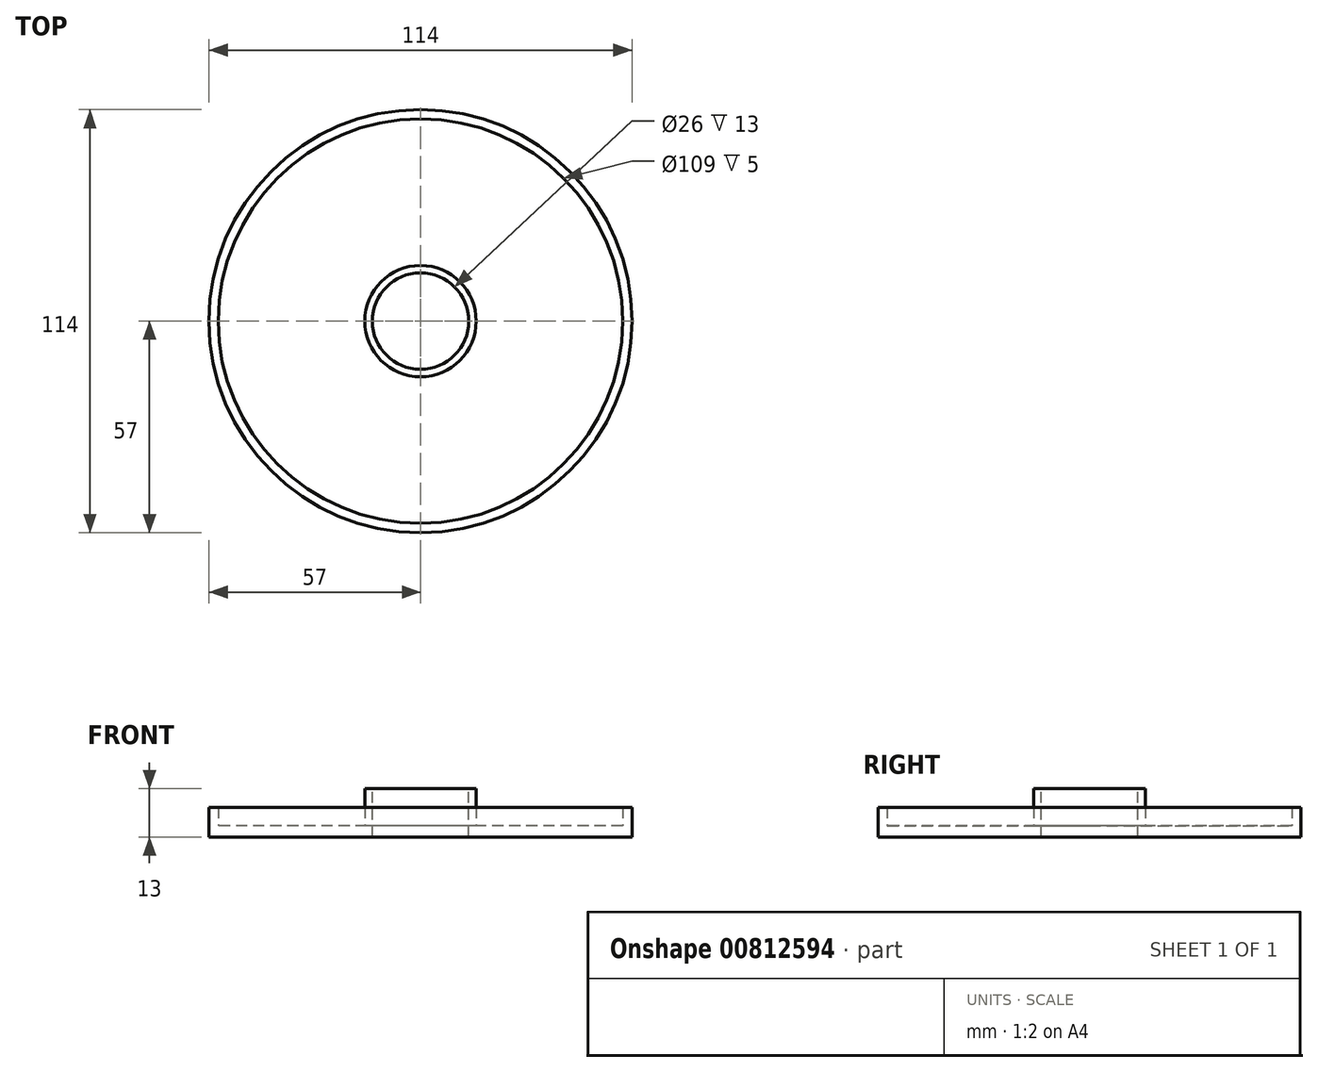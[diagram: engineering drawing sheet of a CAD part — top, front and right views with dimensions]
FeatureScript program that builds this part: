
annotation { "Feature Type Name" : "Feature", "Feature Type Description" : "" }
export const myFeature = defineFeature(function(context is Context, id is Id, definition is map)
    precondition{}
    {
        {
            var Q0;
            Q0=qCreatedBy(makeId("Top.planeOp"),FACE);
            var sketch = newSketch(context, id + "F0", { "sketchPlane" : qUnion([Q0])});
            skCircle(sketch, "E0", {"center": v(0, 0) * mm, "radius": 54.5 * mm});
            skCircle(sketch, "E1", {"center": v(0, 0) * mm, "radius": 57 * mm});
            skCircle(sketch, "E2", {"center": v(0, 0) * mm, "radius": 13 * mm});
            skCircle(sketch, "E3", {"center": v(0, 0) * mm, "radius": 15 * mm});
            skSolve(sketch);
        }
        {
            var Q0;
            Q0=makeQuery(id+"F0.imprint","IMPRINT",FACE,{"disambiguationData":[TD([[makeQuery(id+"F0.imprint","IMPRINT",EDGE,{"derivedFrom":sQuery(id+"F0.wireOp",EDGE,"E0")}),1.0]])]});
            var Q1;
            Q1=makeQuery(id+"F0.imprint","IMPRINT",FACE,{"disambiguationData":[TD([[makeQuery(id+"F0.imprint","IMPRINT",EDGE,{"derivedFrom":sQuery(id+"F0.wireOp",EDGE,"E0")}),-1.0]])]});
            var Q2;
            Q2=makeQuery(id+"F0.imprint","IMPRINT",FACE,{"disambiguationData":[TD([[makeQuery(id+"F0.imprint","IMPRINT",EDGE,{"derivedFrom":sQuery(id+"F0.wireOp",EDGE,"E2")}),-1.0]])]});
            extrude(context, id + "F1", {"entities" : qUnion([Q0, Q1, Q2]), "depth" : -3 * mm, "offsetDistance" : 25 * mm});
        }
        {
            var Q0;
            Q0 = qSketchRegion(id + "F0", true);
            extrude(context, id + "F2", {"entities" : qUnion([Q0]), "operationType" : NewBodyOperationType.ADD, "depth" : 5 * mm, "offsetDistance" : 25 * mm});
        }
        {
            var Q0;
            Q0=makeQuery(id+"F0.imprint","IMPRINT",FACE,{"disambiguationData":[TD([[makeQuery(id+"F0.imprint","IMPRINT",EDGE,{"derivedFrom":sQuery(id+"F0.wireOp",EDGE,"E2")}),-1.0]])]});
            extrude(context, id + "F3", {"entities" : qUnion([Q0]), "operationType" : NewBodyOperationType.ADD, "depth" : 10 * mm, "offsetDistance" : 25 * mm});
        }
    });
